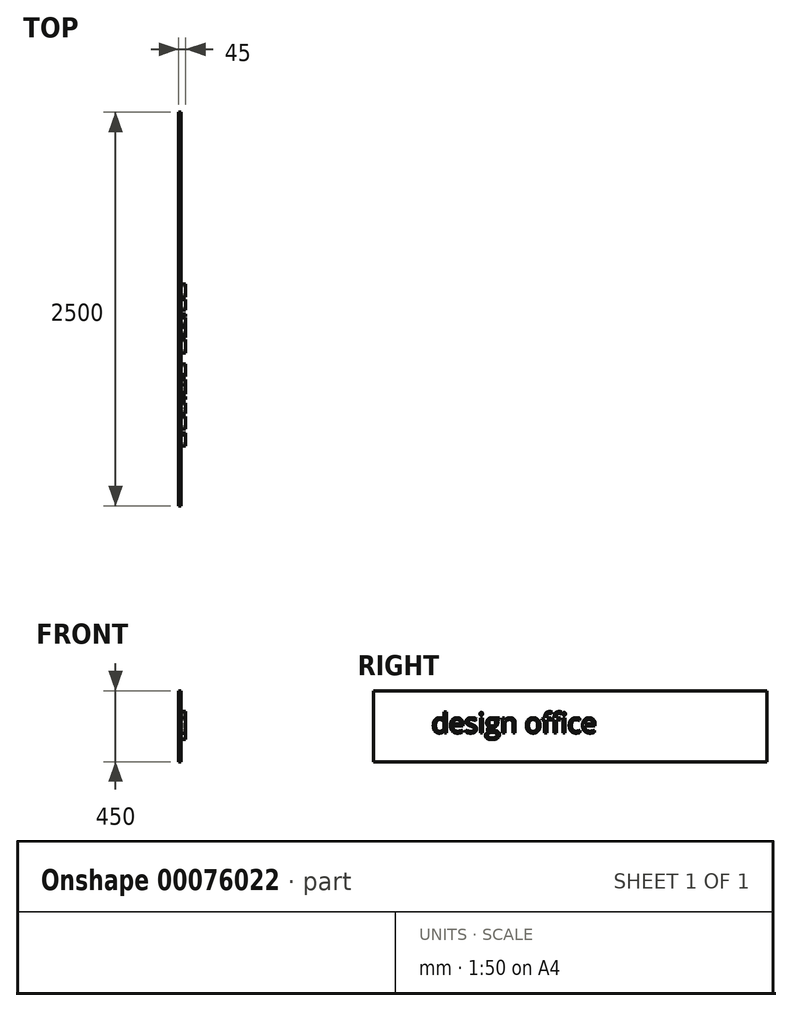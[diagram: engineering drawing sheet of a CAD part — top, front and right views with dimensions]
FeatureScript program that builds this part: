
annotation { "Feature Type Name" : "Feature", "Feature Type Description" : "" }
export const myFeature = defineFeature(function(context is Context, id is Id, definition is map)
    precondition{}
    {
        {
            var Q0;
            Q0=qCreatedBy(makeId("Front.planeOp"),FACE);
            var sketch = newSketch(context, id + "F0", { "sketchPlane" : qUnion([Q0])});
            skLineSegment(sketch, "E0.bottom", {"start": v(4.8, 0) * mm, "end": v(-10.2, 0) * mm});
            skLineSegment(sketch, "E0.top", {"start": v(4.8, 450) * mm, "end": v(-10.2, 450) * mm});
            skLineSegment(sketch, "E0.left", {"start": v(4.8, 0) * mm, "end": v(4.8, 450) * mm});
            skLineSegment(sketch, "E0.right", {"start": v(-10.2, 0) * mm, "end": v(-10.2, 450) * mm});
            skSolve(sketch);
        }
        {
            var Q0;
            Q0=makeQuery(id+"F0.imprint","IMPRINT",FACE,{"disambiguationData":[TD([[makeQuery(id+"F0.imprint","IMPRINT",EDGE,{"derivedFrom":sQuery(id+"F0.wireOp",EDGE,"E0.bottom")}),-1.0]])]});
            extrude(context, id + "F1", {"entities" : qUnion([Q0]), "depth" : 2500 * mm});
        }
        {
            var Q0;
            Q0=makeQuery(id+"F1.opExtrude","SWEPT_FACE",FACE,{"disambiguationData":[OSD([sQuery(id+"F0.wireOp",EDGE,"E0.left")])]});
            var sketch = newSketch(context, id + "F2", { "sketchPlane" : qUnion([Q0])});
            skText(sketch, "E1", { "text": "design office\n", "fontName": "OpenSans-Regular.ttf"});
            const initialGuessF2  = {"E1": [-2.13027, 0.18272, 1, 0, 0.12792]};
            skSetInitialGuess(sketch, initialGuessF2);
            skSolve(sketch);
        }
        {
            var Q0;
            Q0 = qSketchRegion(id + "F2", true);
            extrude(context, id + "F3", {"entities" : qUnion([Q0]), "operationType" : NewBodyOperationType.ADD, "depth" : 30 * mm});
        }
    });
